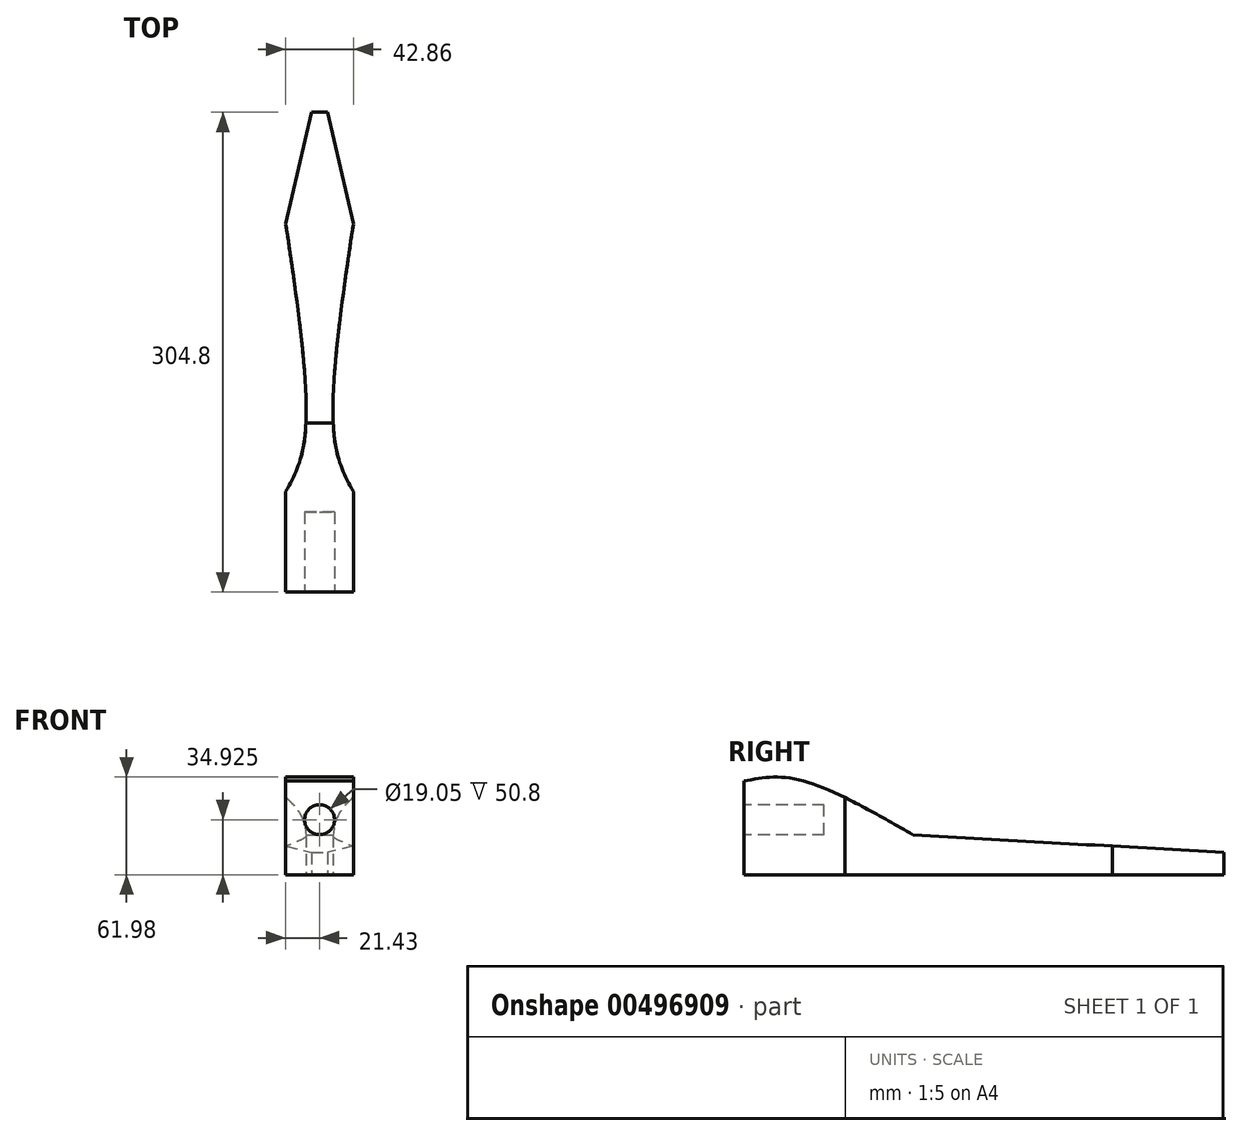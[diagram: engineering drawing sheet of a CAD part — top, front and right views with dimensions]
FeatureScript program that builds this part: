
annotation { "Feature Type Name" : "Feature", "Feature Type Description" : "" }
export const myFeature = defineFeature(function(context is Context, id is Id, definition is map)
    precondition{}
    {
        {
            var Q0;
            Q0=qCreatedBy(makeId("Right.planeOp"),FACE);
            var sketch = newSketch(context, id + "F0", { "sketchPlane" : qUnion([Q0])});
            skLineSegment(sketch, "E0", {"start": v(-152.4, 0) * mm, "end": v(152.4, 0) * mm});
            skLineSegment(sketch, "E1", {"start": v(-152.4, 0) * mm, "end": v(-152.4, 69.85) * mm});
            skLineSegment(sketch, "E2", {"start": v(152.4, 0) * mm, "end": v(152.4, 19.05) * mm});
            skLineSegment(sketch, "E3", {"start": v(152.4, 19.05) * mm, "end": v(-152.4, 69.85) * mm});
            skPoint(sketch, "E4.endSnap0", {"position": v(-152.4, 34.93) * mm});
            skLineSegment(sketch, "E5.0", {"start": v(-95.25, 50.8) * mm, "end": v(-152.4, 50.8) * mm, "construction": true});
            skLineSegment(sketch, "E5.1", {"start": v(-95.25, 50.8) * mm, "end": v(-95.25, 19.05) * mm, "construction": true});
            skLineSegment(sketch, "E5.2", {"start": v(-95.25, 19.05) * mm, "end": v(-152.4, 19.05) * mm, "construction": true});
            skSolve(sketch);
        }
        {
            var Q0;
            Q0=makeQuery(id+"F0.imprint","IMPRINT",FACE,{"disambiguationData":[TD([[makeQuery(id+"F0.imprint","IMPRINT",EDGE,{"derivedFrom":sQuery(id+"F0.wireOp",EDGE,"E0")}),1.0]])]});
            extrude(context, id + "F1", {"entities" : qUnion([Q0]), "depth" : 42.86 * mm, "symmetric" : true});
        }
        {
            var Q0;
            Q0=makeQuery(id+"F1.opExtrude","SWEPT_FACE",FACE,{"disambiguationData":[OSD([sQuery(id+"F0.wireOp",EDGE,"E1")])]});
            var sketch = newSketch(context, id + "F2", { "sketchPlane" : qUnion([Q0])});
            skLineSegment(sketch, "E6", {"start": v(21.43, 34.93) * mm, "end": v(0, 34.93) * mm, "construction": true});
            skCircle(sketch, "E7", {"center": v(0, 34.93) * mm, "radius": 9.53 * mm});
            skSolve(sketch);
        }
        {
            var Q0;
            Q0=makeQuery(id+"F2.imprint","IMPRINT",FACE,{"disambiguationData":[TD([[makeQuery(id+"F2.imprint","IMPRINT",EDGE,{"derivedFrom":sQuery(id+"F2.wireOp",EDGE,"E7")}),1.0]])]});
            var Q1;
            Q1=sQuery(id+"F2.wireOp",EDGE,"E7");
            extrude(context, id + "F3", {"entities" : qUnion([Q0]), "operationType" : NewBodyOperationType.REMOVE, "surfaceEntities" : qUnion([Q1]), "oppositeDirection" : true, "depth" : 50.8 * mm});
        }
        {
            var Q0;
            Q0=makeQuery(id+"F1.opExtrude","CAP_FACE",FACE,{"disambiguationData":[OSD([sQuery(id+"F0.wireOp",EDGE,"E0"),sQuery(id+"F0.wireOp",EDGE,"E1"),sQuery(id+"F0.wireOp",EDGE,"E2"),sQuery(id+"F0.wireOp",EDGE,"E3")])],"isStart":false});
            var sketch = newSketch(context, id + "F4", { "sketchPlane" : qUnion([Q0])});
            skLineSegment(sketch, "E8", {"start": v(-152.4, 34.93) * mm, "end": v(-152.4, 44.45) * mm, "construction": true});
            skLineSegment(sketch, "E9.0", {"start": v(-95.25, 11.11) * mm, "end": v(-152.4, 11.11) * mm, "construction": true});
            skLineSegment(sketch, "E9.1", {"start": v(-95.25, 42.86) * mm, "end": v(-95.25, 11.11) * mm, "construction": true});
            skLineSegment(sketch, "E9.2", {"start": v(-152.4, 42.86) * mm, "end": v(-95.25, 42.86) * mm, "construction": true});
            skLineSegment(sketch, "E10", {"start": v(57.15, 0) * mm, "end": v(57.15, 34.93) * mm, "construction": true});
            skLineSegment(sketch, "E11", {"start": v(-152.4, 44.45) * mm, "end": v(-101.6, 44.45) * mm, "construction": true});
            skLineSegment(sketch, "E12", {"start": v(-101.6, 44.45) * mm, "end": v(-101.6, 25.4) * mm, "construction": true});
            skLineSegment(sketch, "E13", {"start": v(-101.6, 25.4) * mm, "end": v(-152.4, 25.4) * mm, "construction": true});
            skCircle(sketch, "E14", {"center": v(100.56, 9.52) * mm, "radius": 1.59 * mm});
            skCircle(sketch, "E15", {"center": v(-83.78, 9.53) * mm, "radius": 1.59 * mm});
            skFitSpline(sketch, "E16", {"points": [v(-152.4, 59.52) * mm, v(-119.26, 60.66) * mm, v(-45.1, 25.3) * mm], "startDerivative": vector(78.32, 14.74) * mm, "endDerivative": vector(132.27, -76.42) * mm});
            skLineSegment(sketch, "E17", {"start": v(-45.1, 25.3) * mm, "end": v(152.4, 14.17) * mm});
            skLineSegment(sketch, "E18", {"start": v(152.4, 14.17) * mm, "end": v(152.4, 0) * mm});
            skLineSegment(sketch, "E19", {"start": v(152.4, 0) * mm, "end": v(-152.4, 0) * mm});
            skLineSegment(sketch, "E20", {"start": v(-152.4, 0) * mm, "end": v(-152.4, 59.52) * mm});
            skSolve(sketch);
        }
        {
            var Q0;
            Q0=makeQuery(id+"F1.opExtrude","SWEPT_FACE",FACE,{"disambiguationData":[OSD([sQuery(id+"F0.wireOp",EDGE,"E0")])]});
            var sketch = newSketch(context, id + "F5", { "sketchPlane" : qUnion([Q0])});
            skLineSegment(sketch, "E21", {"start": v(0, 152.4) * mm, "end": v(0, -152.4) * mm, "construction": true});
            skLineSegment(sketch, "E22", {"start": v(21.43, -57.15) * mm, "end": v(-21.43, -57.15) * mm, "construction": true});
            skLineSegment(sketch, "E23", {"start": v(15.88, 152.4) * mm, "end": v(15.88, 95.25) * mm, "construction": true});
            skLineSegment(sketch, "E24", {"start": v(15.88, 95.25) * mm, "end": v(-15.87, 95.25) * mm, "construction": true});
            skLineSegment(sketch, "E25", {"start": v(-15.87, 95.25) * mm, "end": v(-15.87, 152.4) * mm, "construction": true});
            skLineSegment(sketch, "E26", {"start": v(0, 152.4) * mm, "end": v(-9.53, 152.4) * mm, "construction": true});
            skLineSegment(sketch, "E27", {"start": v(-9.53, 152.4) * mm, "end": v(-9.53, 101.6) * mm, "construction": true});
            skLineSegment(sketch, "E28", {"start": v(-9.52, 101.6) * mm, "end": v(9.53, 101.6) * mm, "construction": true});
            skLineSegment(sketch, "E29", {"start": v(9.53, 101.6) * mm, "end": v(9.53, 152.4) * mm, "construction": true});
            skFitSpline(sketch, "E30", {"points": [v(-21.43, 88.4) * mm, v(-9.52, 55.48) * mm, v(-21.43, -81.5) * mm], "startDerivative": vector(44.46, -80.05) * mm, "endDerivative": vector(-35.67, -241.96) * mm});
            skLineSegment(sketch, "E31", {"start": v(-21.43, -81.5) * mm, "end": v(-5.2, -152.4) * mm});
            skLineSegment(sketch, "E32.MirrorCS", {"start": v(21.43, -81.5) * mm, "end": v(5.2, -152.4) * mm});
            skFitSpline(sketch, "E33.MirrorCS", {"points": [v(21.43, 88.4) * mm, v(9.52, 55.48) * mm, v(21.43, -81.5) * mm], "startDerivative": vector(-44.46, -80.05) * mm, "endDerivative": vector(35.67, -241.96) * mm});
            skLineSegment(sketch, "E34", {"start": v(-21.43, 88.4) * mm, "end": v(-21.43, 152.4) * mm});
            skLineSegment(sketch, "E35", {"start": v(-21.43, 152.4) * mm, "end": v(21.43, 152.4) * mm});
            skLineSegment(sketch, "E36", {"start": v(21.43, 152.4) * mm, "end": v(21.43, 88.4) * mm});
            skSolve(sketch);
        }
        {
            var Q0;
            {var subQ4=sQuery(id+"F4.wireOp",EDGE,"E16");Q0=makeQuery(id+"F4.imprint","IMPRINT",FACE,{"disambiguationData":[TD([[makeQuery(id+"F4.imprint","IMPRINT",EDGE,{"derivedFrom":subQ4}),1.0]])]});}
            extrude(context, id + "F6", {"entities" : qUnion([Q0]), "operationType" : NewBodyOperationType.REMOVE, "endBound" : BoundingType.THROUGH_ALL, "oppositeDirection" : true, "depth" : 25.4 * mm});
        }
        {
            var Q0;
            Q0=makeQuery(id+"F5.imprint","IMPRINT",FACE,{"disambiguationData":[TD([[makeQuery(id+"F5.imprint","IMPRINT",EDGE,{"derivedFrom":sQuery(id+"F5.wireOp",EDGE,"E30")}),1.0]])]});
            extrude(context, id + "F7", {"entities" : qUnion([Q0]), "operationType" : NewBodyOperationType.INTERSECT, "endBound" : BoundingType.THROUGH_ALL, "oppositeDirection" : true, "depth" : 25.4 * mm});
        }
    });
